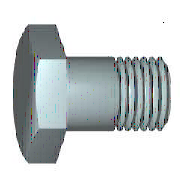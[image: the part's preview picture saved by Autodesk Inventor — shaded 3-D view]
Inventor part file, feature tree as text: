
AUTODESK INVENTOR PART (.ipt)
format: ipt  version: 2022 (Build 260153000, 153)  size: 193,536 bytes
history: native  units: mm (DEFAULTED — no unit token found)
features: sketch x3, extrude x1, chamfer x1, plane x1
ambient origin geometry x7: Origin, YZ Plane, XZ Plane, X Axis, Y Axis, Z Axis, Center Point
bodies: Solid1 (feature_tree), Body (feature_tree)
feature tree (6):
  extrude  "Head"  Depth=22.0mm
  chamfer  "Chamfer1"  Distance=4.7mm
  plane  "Work Plane1"
  sketch  "Sketch1"  dims[d0=40.0mm d1=22.0mm]
  sketch  "Sketch2"  dims[d2=8.0mm]
  sketch  "Sketch4"  dims[d12=90.0deg d3=4.7mm d4=0.0mm d5=30.0deg d21=90.0deg d6=0.766813mm d7=0.766912mm d8=0.0mm d9=0.6001mm d10=11.63mm d11=13.0mm d13=0.766912mm d14=8.0mm d15=22.0mm d16=0.0mm d19=13.0mm d55=45.0deg d57=0.0mm d58=0.0mm]
